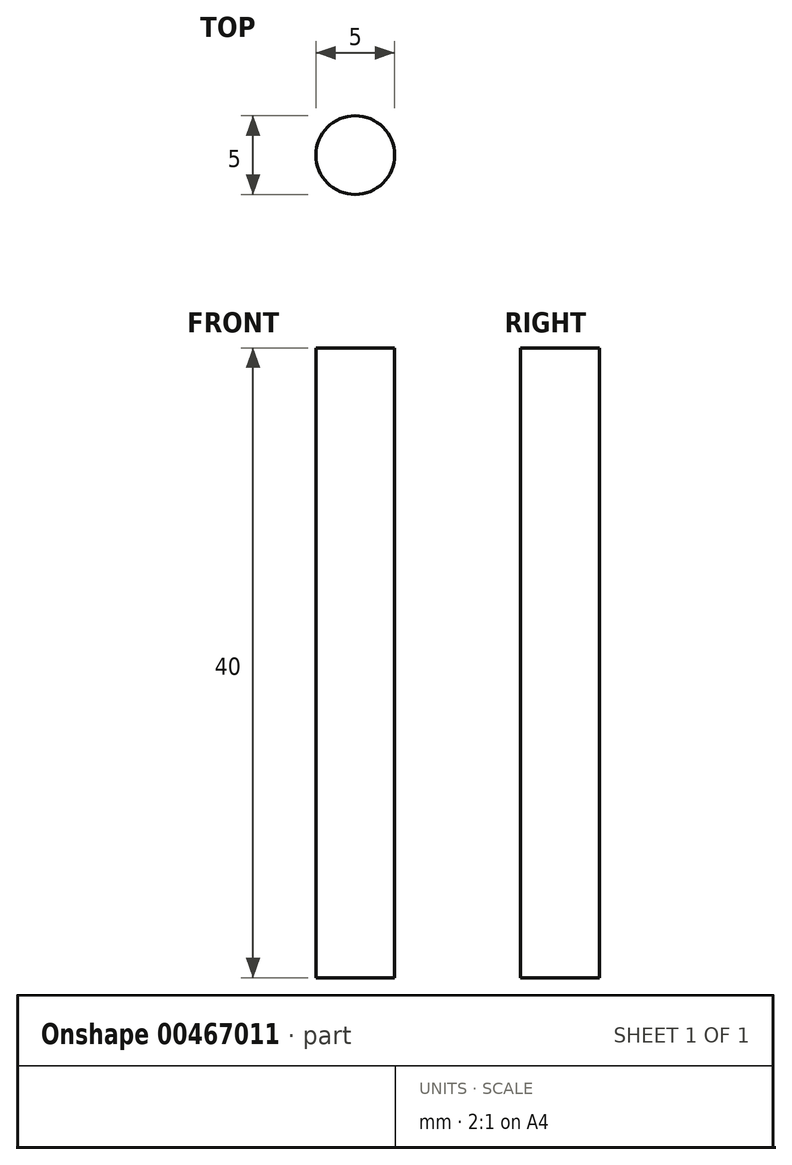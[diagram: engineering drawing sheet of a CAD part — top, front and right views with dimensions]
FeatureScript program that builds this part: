
annotation { "Feature Type Name" : "Feature", "Feature Type Description" : "" }
export const myFeature = defineFeature(function(context is Context, id is Id, definition is map)
    precondition{}
    {
        {
            var Q0;
            Q0=qCreatedBy(makeId("Top.planeOp"),FACE);
            var sketch = newSketch(context, id + "F0", { "sketchPlane" : qUnion([Q0])});
            skCircle(sketch, "E0", {"center": v(0, 0) * mm, "radius": 2.5 * mm});
            skSolve(sketch);
        }
        {
            var Q0;
            Q0=makeQuery(id+"F0.imprint","IMPRINT",FACE,{"disambiguationData":[TD([[makeQuery(id+"F0.imprint","IMPRINT",EDGE,{"derivedFrom":sQuery(id+"F0.wireOp",EDGE,"E0")}),1.0]])]});
            extrude(context, id + "F1", {"entities" : qUnion([Q0]), "depth" : 40 * mm});
        }
    });
